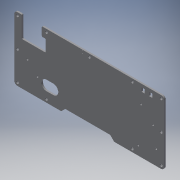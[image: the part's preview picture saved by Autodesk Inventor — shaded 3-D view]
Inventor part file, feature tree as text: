
AUTODESK INVENTOR PART (.ipt)
format: ipt  version: 2019 (Build 230136000, 136)  size: 182,272 bytes
history: native  units: mm
features: extrude x1, sketch x1
ambient origin geometry x8: Origin, YZ Plane, XZ Plane, XY Plane, X Axis, Y Axis, Z Axis, Center Point
bodies: Solid1 (feature_tree)
feature tree (2):
  extrude  "Extrusion1"  [1 undecoded]
  sketch  "Sketch1"  dims[d0=1.6mm d1=0.0mm]
note: 1 required parameter value undecoded (feature->parameter linkage not recoverable at this tier; creation-order binding heuristic only, values carry confidence <= 0.55)
